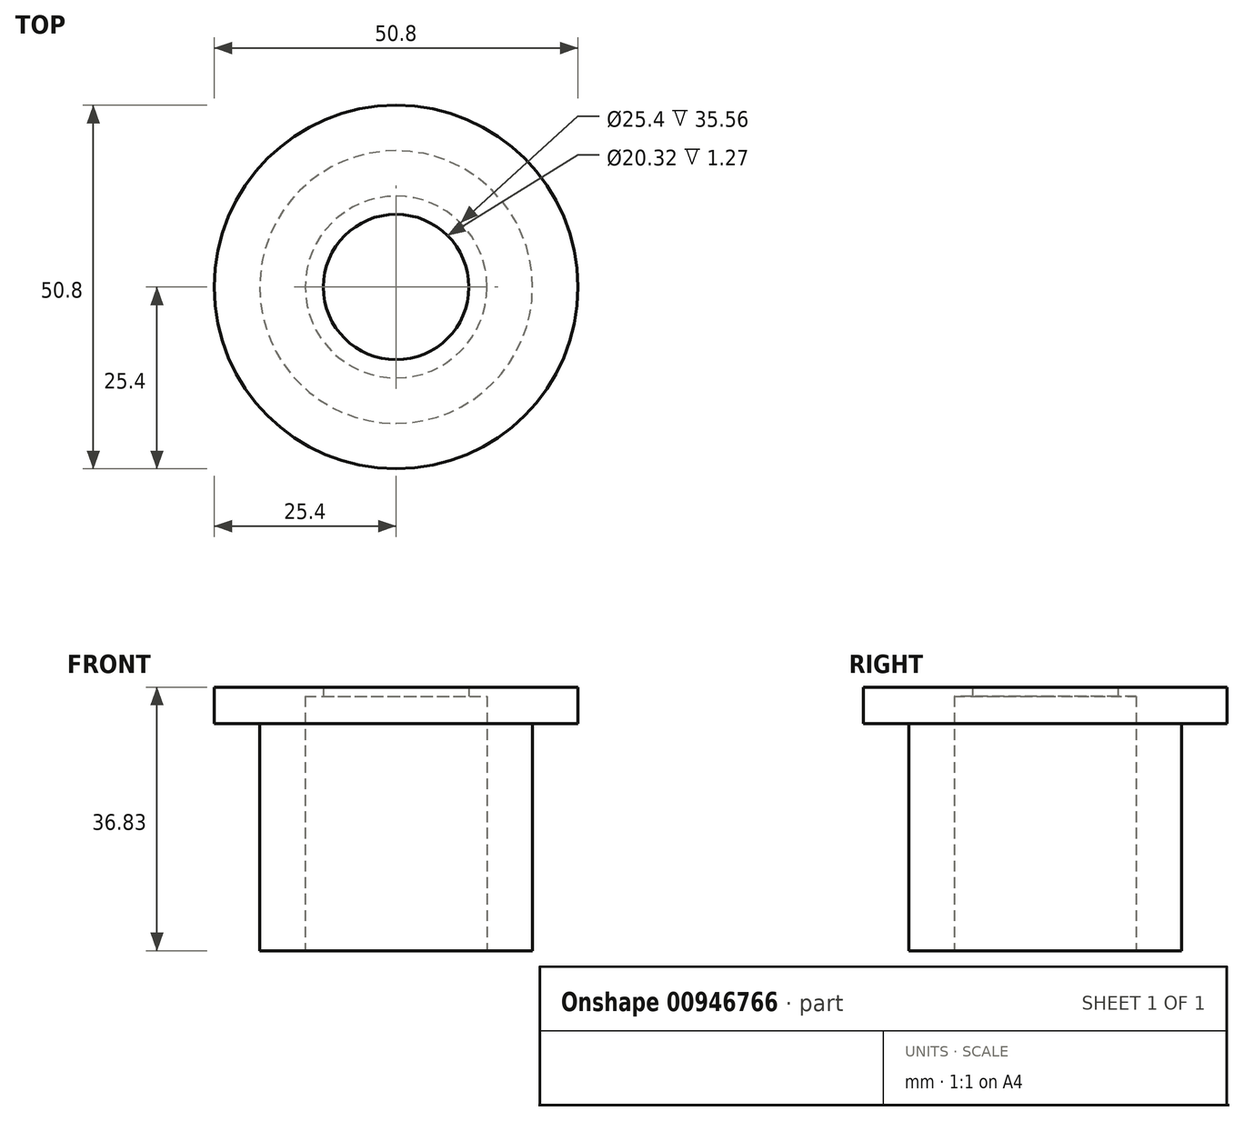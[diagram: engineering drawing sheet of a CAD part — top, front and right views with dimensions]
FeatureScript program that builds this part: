
annotation { "Feature Type Name" : "Feature", "Feature Type Description" : "" }
export const myFeature = defineFeature(function(context is Context, id is Id, definition is map)
    precondition{}
    {
        {
            var Q0;
            Q0=qCreatedBy(makeId("Top.planeOp"),FACE);
            var sketch = newSketch(context, id + "F0", { "sketchPlane" : qUnion([Q0])});
            skCircle(sketch, "E0", {"center": v(0, 0) * mm, "radius": 19.05 * mm});
            skSolve(sketch);
        }
        {
            var Q0;
            Q0 = qSketchRegion(id + "F0", true);
            extrude(context, id + "F1", {"entities" : qUnion([Q0]), "depth" : 31.75 * mm, "offsetDistance" : 25.4 * mm});
        }
        {
            var Q0;
            Q0=makeQuery(id+"F1.opExtrude","CAP_FACE",FACE,{"disambiguationData":[OSD([sQuery(id+"F0.wireOp",EDGE,"E0")])],"isStart":true});
            var sketch = newSketch(context, id + "F2", { "sketchPlane" : qUnion([Q0])});
            skCircle(sketch, "E1", {"center": v(0, 0) * mm, "radius": 10.16 * mm});
            skSolve(sketch);
        }
        {
            var Q0;
            Q0=makeQuery(id+"F1.opExtrude","CAP_FACE",FACE,{"disambiguationData":[OSD([sQuery(id+"F0.wireOp",EDGE,"E0")])],"isStart":true});
            var sketch = newSketch(context, id + "F3", { "sketchPlane" : qUnion([Q0])});
            skCircle(sketch, "E2", {"center": v(0, 0) * mm, "radius": 12.7 * mm});
            skSolve(sketch);
        }
        {
            var Q0;
            Q0=makeQuery(id+"F1.opExtrude","CAP_FACE",FACE,{"disambiguationData":[OSD([sQuery(id+"F0.wireOp",EDGE,"E0")])],"isStart":false});
            var sketch = newSketch(context, id + "F4", { "sketchPlane" : qUnion([Q0])});
            skCircle(sketch, "E3", {"center": v(0, 0) * mm, "radius": 25.4 * mm});
            skSolve(sketch);
        }
        {
            var Q0;
            Q0 = qSketchRegion(id + "F4", true);
            extrude(context, id + "F5", {"entities" : qUnion([Q0]), "operationType" : NewBodyOperationType.ADD, "oppositeDirection" : true, "depth" : 5.08 * mm, "offsetDistance" : 25.4 * mm});
        }
        {
            var Q0;
            Q0 = qSketchRegion(id + "F3", true);
            extrude(context, id + "F6", {"entities" : qUnion([Q0]), "operationType" : NewBodyOperationType.REMOVE, "oppositeDirection" : true, "depth" : 30.48 * mm, "offsetDistance" : 25.4 * mm});
        }
        {
            var Q0;
            Q0 = qSketchRegion(id + "F2", true);
            extrude(context, id + "F7", {"entities" : qUnion([Q0]), "operationType" : NewBodyOperationType.REMOVE, "oppositeDirection" : true, "depth" : 42.67 * mm, "offsetDistance" : 25.4 * mm});
        }
        {
            var Q0;
            Q0=makeQuery(id+"F1.opExtrude","CAP_FACE",FACE,{"disambiguationData":[OSD([sQuery(id+"F0.wireOp",EDGE,"E0")])],"isStart":true});
            extrude(context, id + "F8", {"entities" : qUnion([Q0]), "operationType" : NewBodyOperationType.ADD, "depth" : 5.08 * mm, "offsetDistance" : 25.4 * mm});
        }
    });
